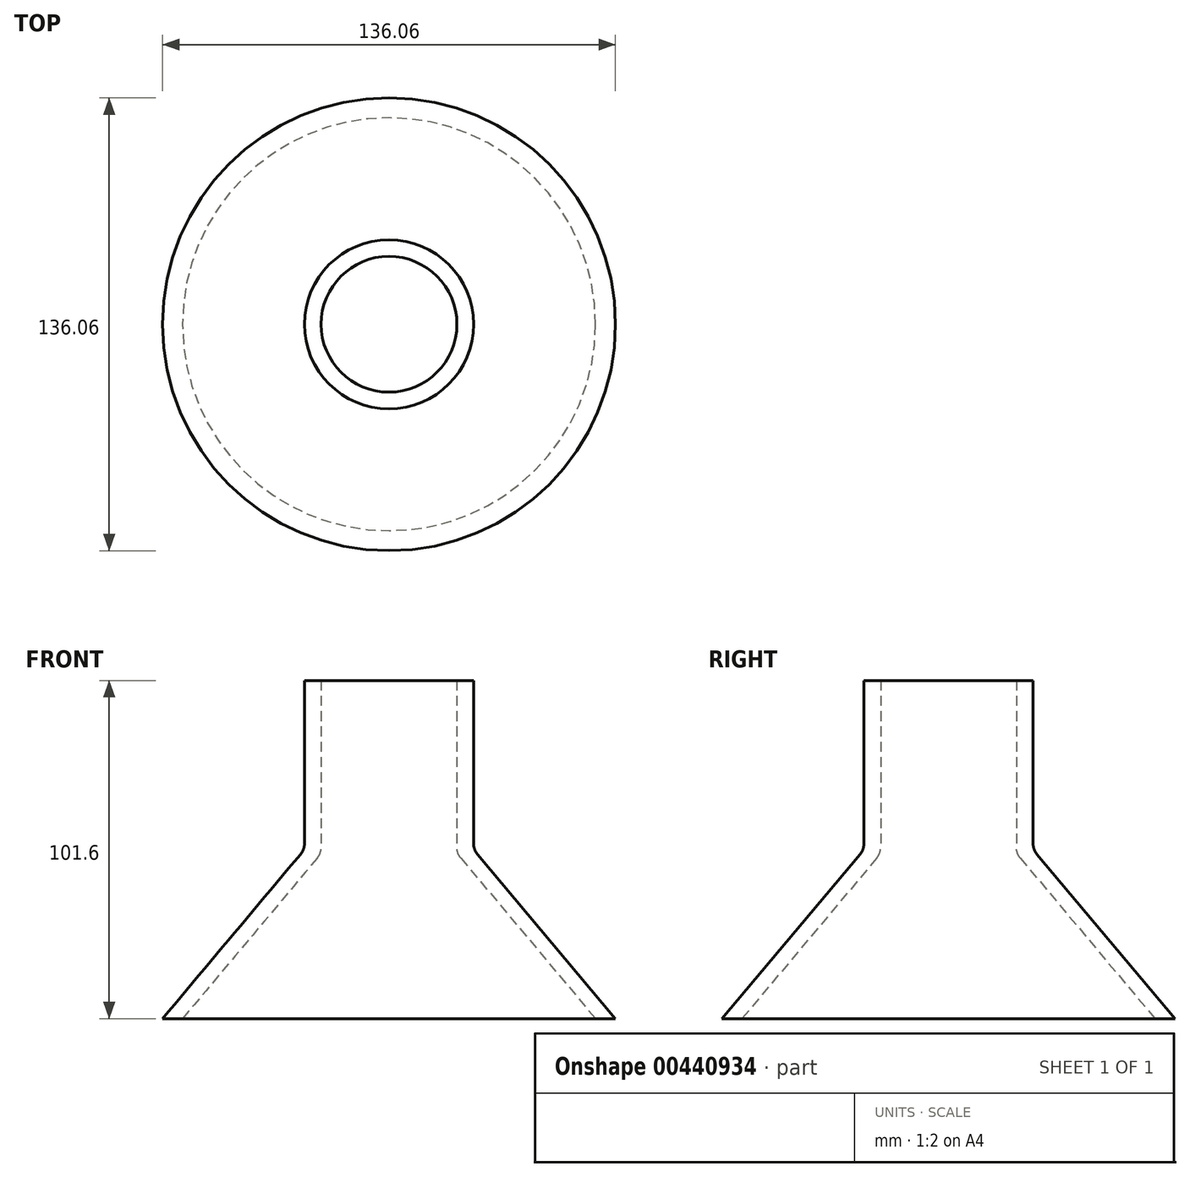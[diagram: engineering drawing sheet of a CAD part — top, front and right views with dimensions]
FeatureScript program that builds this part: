
annotation { "Feature Type Name" : "Feature", "Feature Type Description" : "" }
export const myFeature = defineFeature(function(context is Context, id is Id, definition is map)
    precondition{}
    {
        {
            var Q0;
            Q0=qCreatedBy(makeId("Front.planeOp"),FACE);
            var sketch = newSketch(context, id + "F0", { "sketchPlane" : qUnion([Q0])});
            skLineSegment(sketch, "E0", {"start": v(0, -42.93) * mm, "end": v(0, 45.18) * mm, "construction": true});
            skLineSegment(sketch, "E1", {"start": v(25.4, 86.6) * mm, "end": v(25.4, 37.62) * mm});
            skLineSegment(sketch, "E2", {"start": v(26.57, 34.4) * mm, "end": v(68.03, -15) * mm});
            skLineSegment(sketch, "E3", {"start": v(68.03, -15) * mm, "end": v(62.03, -15) * mm});
            skLineSegment(sketch, "E4", {"start": v(62.03, -15) * mm, "end": v(21.57, 33.21) * mm});
            skLineSegment(sketch, "E5", {"start": v(20.4, 36.43) * mm, "end": v(20.4, 86.6) * mm});
            skLineSegment(sketch, "E6", {"start": v(20.4, 86.6) * mm, "end": v(25.4, 86.6) * mm});
            skPoint(sketch, "E7.visualSharp", {"position": v(20.4, 34.6) * mm});
            skArc(sketch, "E7.filletArc", {"start": v(20.4, 36.43) * mm, "mid": v(20.7, 34.72) * mm, "end": v(21.57, 33.21) * mm});
            skPoint(sketch, "E8.visualSharp", {"position": v(25.4, 35.8) * mm});
            skArc(sketch, "E8.filletArc", {"start": v(25.4, 37.62) * mm, "mid": v(25.7, 35.9) * mm, "end": v(26.57, 34.4) * mm});
            skSolve(sketch);
        }
        {
            var Q0;
            Q0=makeQuery(id+"F0.imprint","IMPRINT",FACE,{"disambiguationData":[TD([[makeQuery(id+"F0.imprint","IMPRINT",EDGE,{"derivedFrom":sQuery(id+"F0.wireOp",EDGE,"E1")}),-1.0]])]});
            var Q1;
            Q1=sQuery(id+"F0.wireOp",EDGE,"E0");
            revolve(context, id + "F1", {"entities" : qUnion([Q0]), "axis" : qUnion([Q1]), "revolveType" : RevolveType.FULL});
        }
    });
